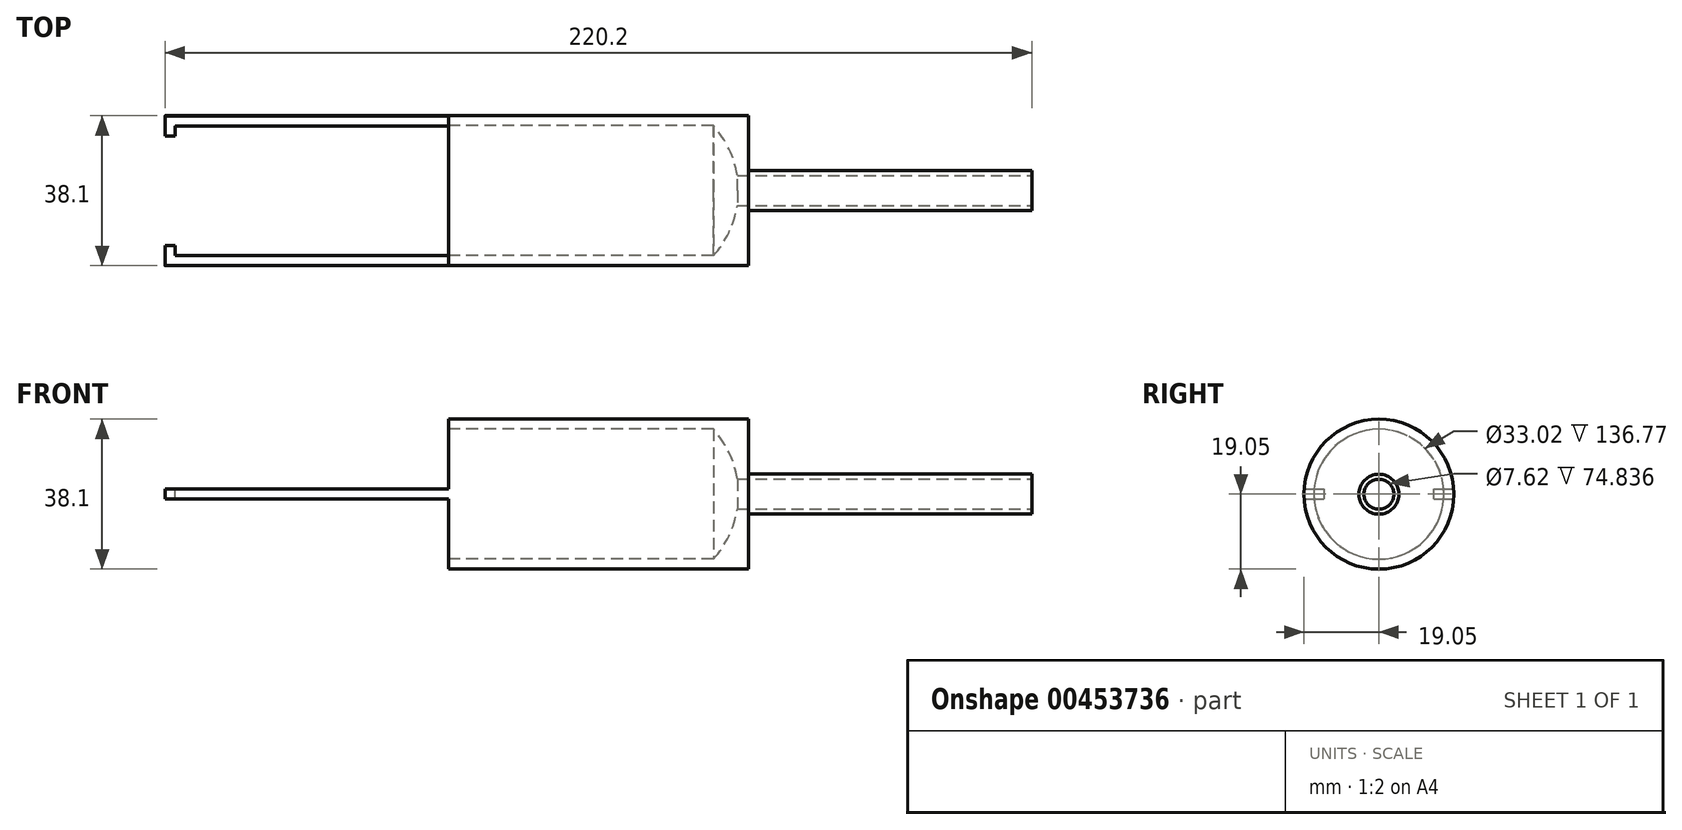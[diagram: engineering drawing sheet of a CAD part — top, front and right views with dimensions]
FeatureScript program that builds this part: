
annotation { "Feature Type Name" : "Feature", "Feature Type Description" : "" }
export const myFeature = defineFeature(function(context is Context, id is Id, definition is map)
    precondition{}
    {
        {
            var Q0;
            Q0=qCreatedBy(makeId("Right.planeOp"),FACE);
            var sketch = newSketch(context, id + "F0", { "sketchPlane" : qUnion([Q0])});
            skCircle(sketch, "E0", {"center": v(0, 0) * mm, "radius": 19.05 * mm});
            skSolve(sketch);
        }
        {
            var Q0;
            Q0=makeQuery(id+"F0.imprint","IMPRINT",FACE,{"disambiguationData":[TD([[makeQuery(id+"F0.imprint","IMPRINT",EDGE,{"derivedFrom":sQuery(id+"F0.wireOp",EDGE,"E0")}),1.0]])]});
            extrude(context, id + "F1", {"entities" : qUnion([Q0]), "oppositeDirection" : true, "depth" : 76.2 * mm + 72 * mm});
        }
        {
            var Q0;
            Q0=qCreatedBy(makeId("Front.planeOp"),FACE);
            var sketch = newSketch(context, id + "F2", { "sketchPlane" : qUnion([Q0])});
            skLineSegment(sketch, "E1", {"start": v(0, 0) * mm, "end": v(-2.54, 0) * mm});
            skLineSegment(sketch, "E2", {"start": v(-2.54, 0) * mm, "end": v(-8.9, 0) * mm});
            skLineSegment(sketch, "E3", {"start": v(-8.9, 0) * mm, "end": v(-148.2, 0) * mm});
            skLineSegment(sketch, "E4", {"start": v(-8.9, 0) * mm, "end": v(-8.9, -16.51) * mm});
            skLineSegment(sketch, "E5", {"start": v(-8.89, -16.51) * mm, "end": v(-76.2, -16.51) * mm});
            skLineSegment(sketch, "E6", {"start": v(-148.2, -16.51) * mm, "end": v(-148.2, 0) * mm});
            skArc(sketch, "E7", {"start": v(-8.89, -16.51) * mm, "mid": v(-4.18, -8.84) * mm, "end": v(-2.54, 0) * mm});
            skPoint(sketch, "E8", {"position": v(-76.2, -16.51) * mm});
            skLineSegment(sketch, "E9", {"start": v(-76.2, -16.51) * mm, "end": v(-145.66, -16.51) * mm});
            skPoint(sketch, "E10.start.orphan", {"position": v(-152.38, -16.51) * mm});
            skLineSegment(sketch, "E11", {"start": v(-145.66, -16.51) * mm, "end": v(-145.66, -13.97) * mm});
            skLineSegment(sketch, "E12", {"start": v(-145.66, -13.97) * mm, "end": v(-148.2, -13.97) * mm});
            skSolve(sketch);
        }
        {
            var Q0;
            Q0 = qSketchRegion(id + "F2", true);
            var Q1;
            Q1=sQuery(id+"F2.wireOp",EDGE,"E3");
            revolve(context, id + "F3", {"operationType" : NewBodyOperationType.REMOVE, "entities" : qUnion([Q0]), "axis" : qUnion([Q1]), "revolveType" : RevolveType.FULL, "oppositeDirection" : true});
        }
        {
            var Q0;
            Q0=qCreatedBy(makeId("Front.planeOp"),FACE);
            var sketch = newSketch(context, id + "F4", { "sketchPlane" : qUnion([Q0])});
            skLineSegment(sketch, "E13", {"start": v(0, 0) * mm, "end": v(-177.8, 0) * mm});
            skLineSegment(sketch, "E14", {"start": v(-76.2, 0) * mm, "end": v(-76.2, 1.27) * mm});
            skLineSegment(sketch, "E15", {"start": v(-76.2, 1.27) * mm, "end": v(-177.8, 1.27) * mm});
            skLineSegment(sketch, "E16", {"start": v(-177.8, 1.27) * mm, "end": v(-177.8, 0) * mm});
            skLineSegment(sketch, "E17", {"start": v(-76.2, 0) * mm, "end": v(-76.2, -1.27) * mm});
            skLineSegment(sketch, "E18", {"start": v(-76.2, -1.27) * mm, "end": v(-177.8, -1.27) * mm});
            skLineSegment(sketch, "E19", {"start": v(-177.8, -1.27) * mm, "end": v(-177.8, 0) * mm});
            skLineSegment(sketch, "E20", {"start": v(-76.2, 1.27) * mm, "end": v(-76.2, 26.05) * mm});
            skLineSegment(sketch, "E21", {"start": v(-76.2, 26.05) * mm, "end": v(-179, 26.05) * mm});
            skLineSegment(sketch, "E22", {"start": v(-179, 26.05) * mm, "end": v(-177.8, 1.27) * mm});
            skLineSegment(sketch, "E23", {"start": v(-177.8, -1.27) * mm, "end": v(-177.8, -33.07) * mm});
            skLineSegment(sketch, "E24", {"start": v(-177.8, -33.07) * mm, "end": v(-76.2, -33.07) * mm});
            skLineSegment(sketch, "E25", {"start": v(-76.2, -33.07) * mm, "end": v(-76.2, -1.27) * mm});
            skSolve(sketch);
        }
        {
            var Q0;
            Q0=makeQuery(id+"F4.imprint","IMPRINT",FACE,{"disambiguationData":[TD([[makeQuery(id+"F4.imprint","IMPRINT",EDGE,{"derivedFrom":sQuery(id+"F4.wireOp",EDGE,"E15")}),-1.0]])]});
            var Q1;
            Q1=makeQuery(id+"F4.imprint","IMPRINT",FACE,{"disambiguationData":[TD([[makeQuery(id+"F4.imprint","IMPRINT",EDGE,{"derivedFrom":sQuery(id+"F4.wireOp",EDGE,"E18")}),1.0]])]});
            extrude(context, id + "F5", {"entities" : qUnion([Q0, Q1]), "operationType" : NewBodyOperationType.REMOVE, "endBound" : BoundingType.SYMMETRIC, "depth" : 50.8 * mm});
        }
        {
            var Q0;
            Q0=makeQuery(id+"F1.opExtrude","CAP_FACE",FACE,{"disambiguationData":[OSD([sQuery(id+"F0.wireOp",EDGE,"E0")])],"isStart":true});
            var sketch = newSketch(context, id + "F6", { "sketchPlane" : qUnion([Q0])});
            skCircle(sketch, "E26", {"center": v(0, 0) * mm, "radius": 5.08 * mm});
            skSolve(sketch);
        }
        {
            var Q0;
            Q0=makeQuery(id+"F6.imprint","IMPRINT",FACE,{"disambiguationData":[TD([[makeQuery(id+"F6.imprint","IMPRINT",EDGE,{"derivedFrom":sQuery(id+"F6.wireOp",EDGE,"E26")}),1.0]])]});
            extrude(context, id + "F7", {"entities" : qUnion([Q0]), "operationType" : NewBodyOperationType.ADD, "depth" : 72 * mm});
        }
        {
            var Q0;
            Q0=makeQuery(id+"F7.opExtrude","CAP_FACE",FACE,{"disambiguationData":[OSD([sQuery(id+"F6.wireOp",EDGE,"E26")])],"isStart":false});
            var sketch = newSketch(context, id + "F8", { "sketchPlane" : qUnion([Q0])});
            skCircle(sketch, "E27", {"center": v(0, 0) * mm, "radius": 3.81 * mm});
            skSolve(sketch);
        }
        {
            var Q0;
            Q0=makeQuery(id+"F8.imprint","IMPRINT",FACE,{"disambiguationData":[TD([[makeQuery(id+"F8.imprint","IMPRINT",EDGE,{"derivedFrom":sQuery(id+"F8.wireOp",EDGE,"E27")}),1.0]])]});
            extrude(context, id + "F9", {"entities" : qUnion([Q0]), "operationType" : NewBodyOperationType.REMOVE, "oppositeDirection" : true, "depth" : 152.4 * mm});
        }
    });
